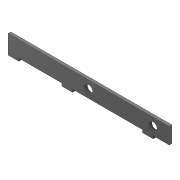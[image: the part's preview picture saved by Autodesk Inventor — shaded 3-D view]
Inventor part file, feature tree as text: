
AUTODESK INVENTOR PART (.ipt)
format: ipt  version: 2020 (Build 240168000, 168)  size: 126,464 bytes
history: native  units: mm
features: extrude x3, sketch x3
ambient origin geometry x8: Origin, YZ Plane, XZ Plane, XY Plane, X Axis, Y Axis, Z Axis, Center Point
bodies: Solid1 (feature_tree)
feature tree (6):
  extrude  "Base"  Depth=30.0mm
  extrude  "Encaixe"  Depth=20.0mm
  extrude  "Extrusion3"  Depth=50.0mm
  sketch  "Sketch1"  dims[d0=300.0mm d1=30.0mm]
  sketch  "Sketch2"  dims[d2=5.0mm d3=0.0mm d4=20.0mm]
  sketch  "Sketch3"  dims[d5=5.0mm d6=60.0mm d8=50.0mm d9=10.0mm d11=10.0mm d13=5.0mm d14=0.0mm d16=15.0mm d17=15.0mm d18=10.0mm d19=0.0mm d20=30.0mm]
